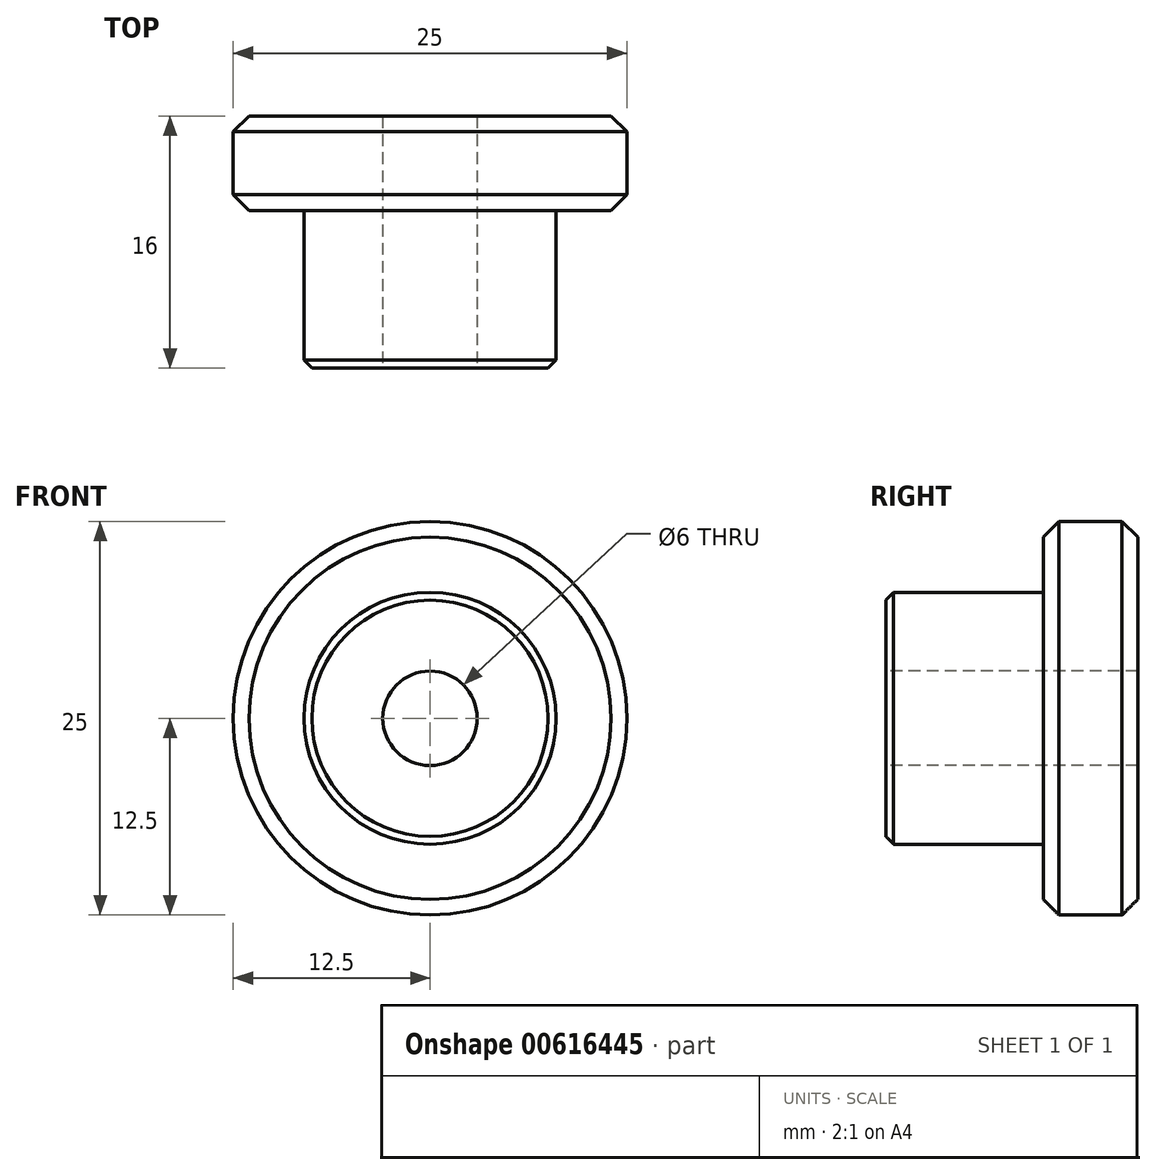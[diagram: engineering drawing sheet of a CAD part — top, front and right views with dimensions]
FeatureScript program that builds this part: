
annotation { "Feature Type Name" : "Feature", "Feature Type Description" : "" }
export const myFeature = defineFeature(function(context is Context, id is Id, definition is map)
    precondition{}
    {
        {
            var Q0;
            Q0=qCreatedBy(makeId("Front.planeOp"),FACE);
            var sketch = newSketch(context, id + "F0", { "sketchPlane" : qUnion([Q0])});
            skCircle(sketch, "E0", {"center": v(0, 0) * mm, "radius": 12.5 * mm});
            skSolve(sketch);
        }
        {
            var Q0;
            Q0 = qSketchRegion(id + "F0", true);
            extrude(context, id + "F1", {"entities" : qUnion([Q0]), "depth" : 6 * mm, "offsetDistance" : 25 * mm});
        }
        {
            var Q0;
            Q0=makeQuery(id+"F1.opExtrude","CAP_FACE",FACE,{"disambiguationData":[OSD([sQuery(id+"F0.wireOp",EDGE,"E0")])],"isStart":false});
            var sketch = newSketch(context, id + "F2", { "sketchPlane" : qUnion([Q0])});
            skCircle(sketch, "E1", {"center": v(0, 0) * mm, "radius": 8 * mm});
            skSolve(sketch);
        }
        {
            var Q0;
            Q0 = qSketchRegion(id + "F2", true);
            extrude(context, id + "F3", {"entities" : qUnion([Q0]), "operationType" : NewBodyOperationType.ADD, "depth" : 10 * mm, "offsetDistance" : 25 * mm});
        }
        {
            var Q0;
            Q0=makeQuery(id+"F3.opExtrude","CAP_FACE",FACE,{"disambiguationData":[OSD([sQuery(id+"F2.wireOp",EDGE,"E1")])],"isStart":false});
            var sketch = newSketch(context, id + "F4", { "sketchPlane" : qUnion([Q0])});
            skCircle(sketch, "E2", {"center": v(0, 0) * mm, "radius": 3 * mm});
            skSolve(sketch);
        }
        {
            var Q0;
            Q0 = qSketchRegion(id + "F4", true);
            extrude(context, id + "F5", {"entities" : qUnion([Q0]), "operationType" : NewBodyOperationType.REMOVE, "oppositeDirection" : true, "depth" : 25 * mm, "offsetDistance" : 25 * mm});
        }
        {
            var Q0;
            Q0=makeQuery(id+"F1.opExtrude","CAP_EDGE",EDGE,{"disambiguationData":[OSD([sQuery(id+"F0.wireOp",EDGE,"E0")])],"isStart":false});
            var Q1;
            Q1=makeQuery(id+"F1.opExtrude","CAP_EDGE",EDGE,{"disambiguationData":[OSD([sQuery(id+"F0.wireOp",EDGE,"E0")])],"isStart":true});
            chamfer(context, id + "F6", {"entities" : qUnion([Q0, Q1]), "width" : 1 * mm, "tangentPropagation" : true});
        }
        {
            var Q0;
            Q0=makeQuery(id+"F3.opExtrude","CAP_EDGE",EDGE,{"disambiguationData":[OSD([sQuery(id+"F2.wireOp",EDGE,"E1")])],"isStart":false});
            chamfer(context, id + "F7", {"entities" : qUnion([Q0]), "width" : .5 * mm, "tangentPropagation" : true});
        }
    });
